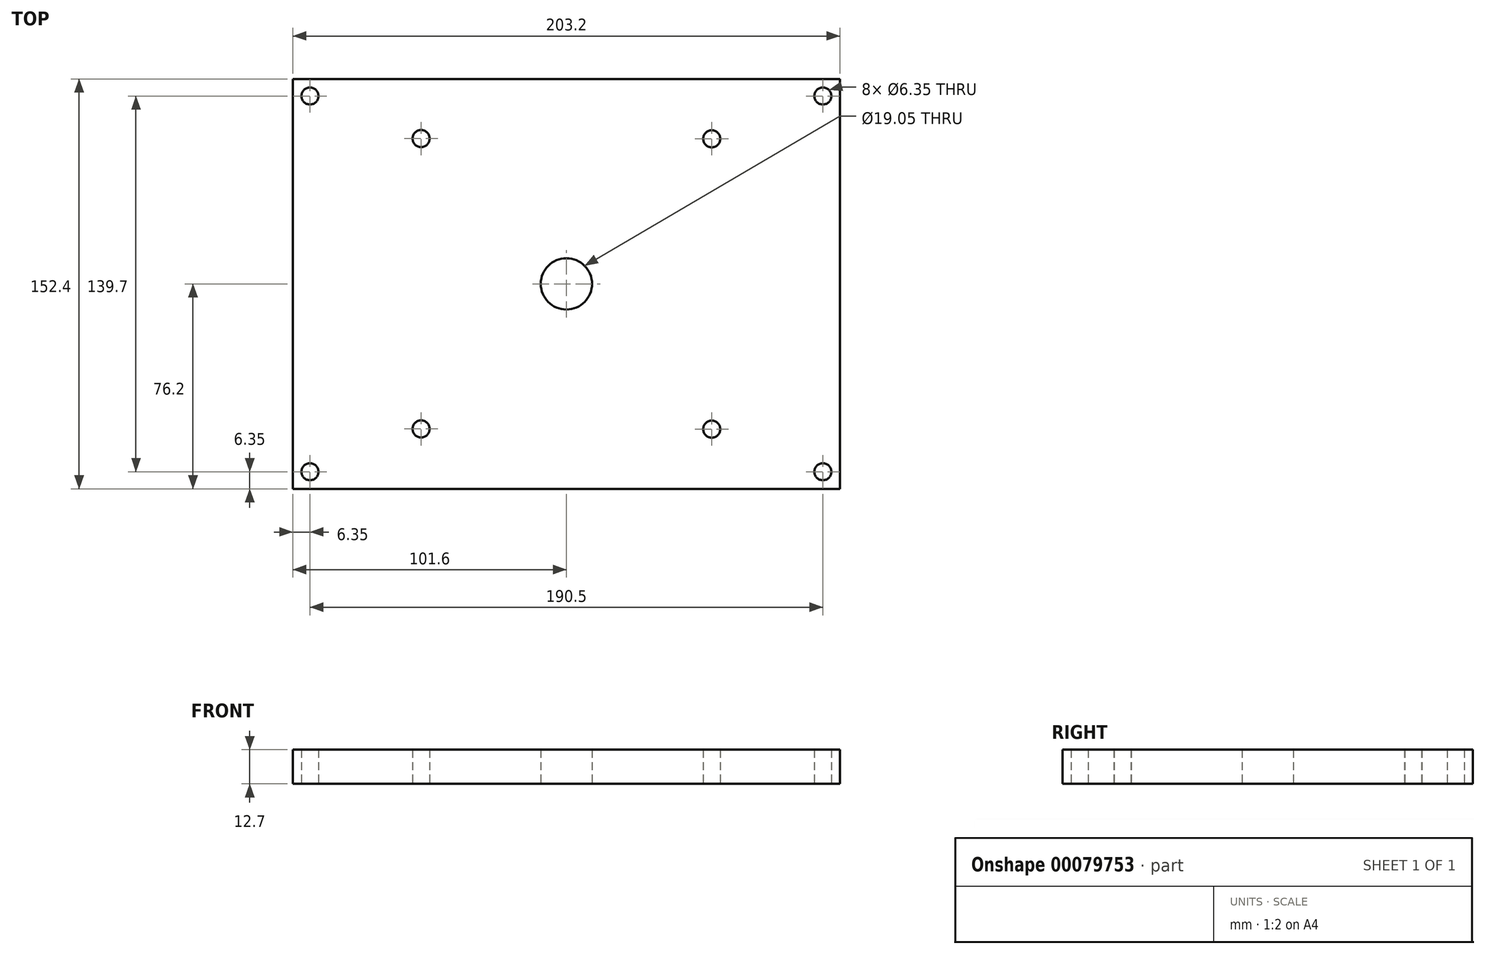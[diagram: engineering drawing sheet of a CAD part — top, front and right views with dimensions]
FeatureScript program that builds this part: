
annotation { "Feature Type Name" : "Feature", "Feature Type Description" : "" }
export const myFeature = defineFeature(function(context is Context, id is Id, definition is map)
    precondition{}
    {
        {
            var Q0;
            Q0=qCreatedBy(makeId("Top.planeOp"),FACE);
            var sketch = newSketch(context, id + "F0", { "sketchPlane" : qUnion([Q0])});
            skLineSegment(sketch, "E0.bottom", {"start": v(101.6, 76.2) * mm, "end": v(-101.6, 76.2) * mm});
            skLineSegment(sketch, "E0.top", {"start": v(101.6, -76.2) * mm, "end": v(-101.6, -76.2) * mm});
            skLineSegment(sketch, "E0.left", {"start": v(101.6, 76.2) * mm, "end": v(101.6, -76.2) * mm});
            skLineSegment(sketch, "E0.right", {"start": v(-101.6, 76.2) * mm, "end": v(-101.6, -76.2) * mm});
            skPoint(sketch, "E0.middle", {"position": v(0, 0) * mm});
            skCircle(sketch, "E1", {"center": v(-53.98, 54.01) * mm, "radius": 3.18 * mm});
            skCircle(sketch, "E2", {"center": v(53.97, 53.94) * mm, "radius": 3.18 * mm});
            skCircle(sketch, "E3", {"center": v(53.98, -54.01) * mm, "radius": 3.18 * mm});
            skCircle(sketch, "E4", {"center": v(-53.98, -53.94) * mm, "radius": 3.18 * mm});
            skCircle(sketch, "E5", {"center": v(-95.25, 69.85) * mm, "radius": 3.18 * mm});
            skCircle(sketch, "E6", {"center": v(95.25, 69.85) * mm, "radius": 3.18 * mm});
            skCircle(sketch, "E7", {"center": v(95.25, -69.85) * mm, "radius": 3.18 * mm});
            skCircle(sketch, "E8", {"center": v(-95.25, -69.85) * mm, "radius": 3.18 * mm});
            skCircle(sketch, "E9", {"center": v(0, 0) * mm, "radius": 9.53 * mm});
            skSolve(sketch);
        }
        {
            var Q0;
            Q0 = qSketchRegion(id + "F0", true);
            extrude(context, id + "F1", {"entities" : qUnion([Q0]), "depth" : 12.7 * mm});
        }
    });
